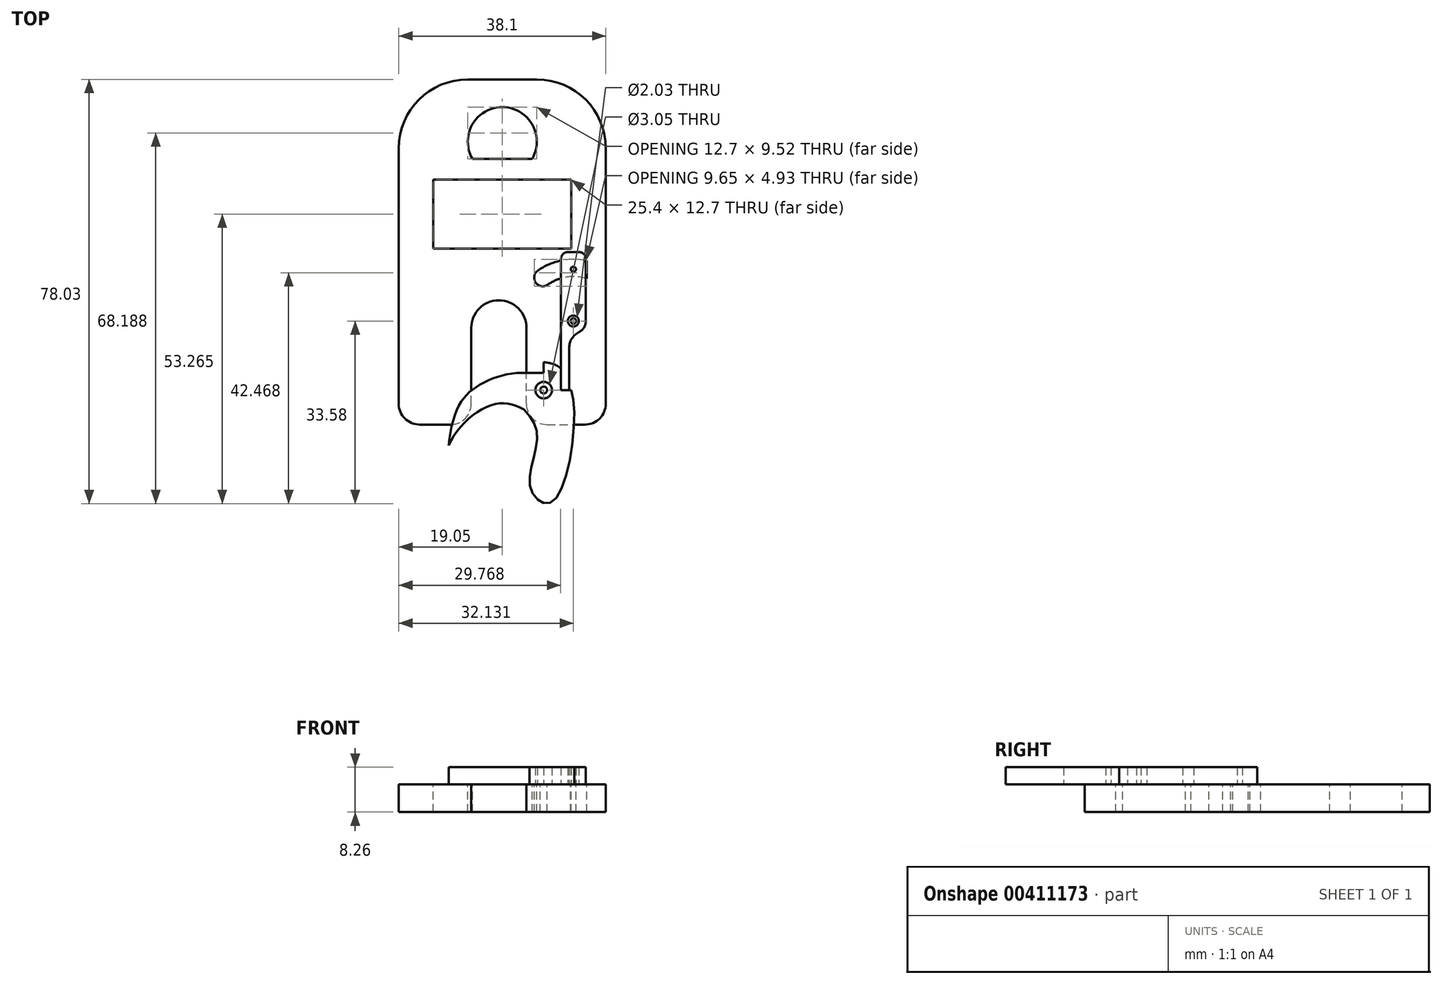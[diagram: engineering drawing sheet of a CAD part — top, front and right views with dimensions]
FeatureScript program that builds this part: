
annotation { "Feature Type Name" : "Feature", "Feature Type Description" : "" }
export const myFeature = defineFeature(function(context is Context, id is Id, definition is map)
    precondition{}
    {
        {
            var Q0;
            Q0=qCreatedBy(makeId("Top.planeOp"),FACE);
            var sketch = newSketch(context, id + "F0", { "sketchPlane" : qUnion([Q0])});
            skCircle(sketch, "E0", {"center": v(0, 0) * mm, "radius": 15.88 * mm, "construction": true});
            skEllipse(sketch, "E1", {"center": v(0, 0) * mm, "majorRadius": 12.7 * mm, "minorRadius": 7.62 * mm, "majorAxis": v(0.7, 0.7), "construction": true});
            skCircle(sketch, "E2", {"center": v(7.62, 7.62) * mm, "radius": 1.52 * mm});
            skLineSegment(sketch, "E3", {"start": v(-8.98, -8.98) * mm, "end": v(8.98, 8.98) * mm, "construction": true});
            skCircle(sketch, "E4", {"center": v(7.62, 7.62) * mm, "radius": 5.1 * mm, "construction": true});
            skLineSegment(sketch, "E5", {"start": v(12.72, 7.62) * mm, "end": v(10.8, 7.62) * mm});
            skLineSegment(sketch, "E6", {"start": v(10.8, 7.62) * mm, "end": v(10.8, 11.6) * mm});
            skArc(sketch, "E7", {"start": v(10.8, 11.6) * mm, "mid": v(9.3, 12.43) * mm, "end": v(7.62, 12.72) * mm});
            skCircle(sketch, "E8", {"center": v(7.62, 7.62) * mm, "radius": 2.98 * mm, "construction": true});
            skCircle(sketch, "E9", {"center": v(7.62, 7.62) * mm, "radius": 21.04 * mm, "construction": true});
            skFitSpline(sketch, "E10", {"points": [v(4.01, 4.01) * mm, v(-2.71, 1.83) * mm, v(-6.43, -8.04) * mm, v(-6.6, -9.02) * mm, v(-8.92, -8.19) * mm, v(-8.76, 2.93) * mm, v(-4.46, 8.4) * mm, v(3.63, 10.8) * mm], "startDerivative": vector(-47.69, -1.45) * mm, "endDerivative": vector(53.95, 0) * mm});
            skFitSpline(sketch, "E11.trimOffspring", {"points": [v(-10.38, -6.12) * mm, v(-1.13, 5.08) * mm, v(3.97, 4.05) * mm, v(4.01, 4.01) * mm, v(6.36, 0) * mm, v(5.13, -10.16) * mm, v(9.24, -12.9) * mm, v(12.72, 7.62) * mm], "startDerivative": vector(-10.72, 64.76) * mm, "endDerivative": vector(-17.22, 48.63) * mm});
            skLineSegment(sketch, "E12", {"start": v(3.63, 10.8) * mm, "end": v(7.62, 10.8) * mm});
            skLineSegment(sketch, "E13", {"start": v(7.62, 12.72) * mm, "end": v(7.62, 10.8) * mm});
            skLineSegment(sketch, "E14", {"start": v(7.62, 7.62) * mm, "end": v(7.62, 14.2) * mm, "construction": true});
            skSolve(sketch);
        }
        {
            var Q0;
            Q0=makeQuery(id+"F0.imprint","IMPRINT",FACE,{"disambiguationData":[TD([[makeQuery(id+"F0.imprint","IMPRINT",EDGE,{"derivedFrom":sQuery(id+"F0.wireOp",EDGE,"E2")}),-1.0]])]});
            extrude(context, id + "F1", {"entities" : qUnion([Q0]), "depth" : 3.17 * mm});
        }
        {
            var Q0;
            Q0=qCreatedBy(makeId("Top.planeOp"),FACE);
            var sketch = newSketch(context, id + "F2", { "sketchPlane" : qUnion([Q0])});
            skLineSegment(sketch, "E15.bottom", {"start": v(-6.35, 64.77) * mm, "end": v(6.35, 64.77) * mm});
            skLineSegment(sketch, "E15.top", {"start": v(-15.24, 1.27) * mm, "end": v(-9.53, 1.27) * mm});
            skLineSegment(sketch, "E15.left", {"start": v(-19.05, 52.07) * mm, "end": v(-19.05, 5.08) * mm});
            skLineSegment(sketch, "E15.right", {"start": v(19.05, 52.07) * mm, "end": v(19.05, 5.08) * mm});
            skLineSegment(sketch, "E16.top", {"start": v(-5.72, 19.05) * mm, "end": v(4.44, 19.05) * mm});
            skLineSegment(sketch, "E16.left", {"start": v(-5.72, 5.08) * mm, "end": v(-5.72, 19.05) * mm});
            skLineSegment(sketch, "E16.right", {"start": v(4.45, 5.08) * mm, "end": v(4.44, 19.05) * mm});
            skLineSegment(sketch, "E17", {"start": v(0, 0) * mm, "end": v(0, 39.33) * mm, "construction": true});
            skLineSegment(sketch, "E18.trimOffspring", {"start": v(8.26, 1.27) * mm, "end": v(15.24, 1.27) * mm});
            skCircle(sketch, "E19", {"center": v(7.62, 7.62) * mm, "radius": 0.64 * mm});
            skPoint(sketch, "E20.visualSharp", {"position": v(-19.05, 64.77) * mm});
            skArc(sketch, "E20.filletArc", {"start": v(-6.35, 64.77) * mm, "mid": v(-15.33, 61.05) * mm, "end": v(-19.05, 52.07) * mm});
            skPoint(sketch, "E21.visualSharp", {"position": v(19.05, 64.77) * mm});
            skArc(sketch, "E21.filletArc", {"start": v(19.05, 52.07) * mm, "mid": v(15.33, 61.05) * mm, "end": v(6.35, 64.77) * mm});
            skArc(sketch, "E22", {"start": v(5.5, 50.17) * mm, "mid": v(0, 59.7) * mm, "end": v(-5.5, 50.17) * mm});
            skLineSegment(sketch, "E23", {"start": v(-5.5, 50.17) * mm, "end": v(5.5, 50.17) * mm});
            skArc(sketch, "E24", {"start": v(4.44, 19.05) * mm, "mid": v(-0.64, 24.13) * mm, "end": v(-5.72, 19.05) * mm});
            skPoint(sketch, "E25.visualSharp", {"position": v(-19.05, 1.27) * mm});
            skArc(sketch, "E25.filletArc", {"start": v(-19.05, 5.08) * mm, "mid": v(-17.93, 2.39) * mm, "end": v(-15.24, 1.27) * mm});
            skPoint(sketch, "E26.visualSharp", {"position": v(-5.72, 1.27) * mm});
            skArc(sketch, "E26.filletArc", {"start": v(-9.53, 1.27) * mm, "mid": v(-6.83, 2.39) * mm, "end": v(-5.72, 5.08) * mm});
            skPoint(sketch, "E27.visualSharp", {"position": v(4.45, 1.27) * mm});
            skArc(sketch, "E27.filletArc", {"start": v(4.45, 5.08) * mm, "mid": v(5.56, 2.39) * mm, "end": v(8.26, 1.27) * mm});
            skPoint(sketch, "E28.visualSharp", {"position": v(19.05, 1.27) * mm});
            skArc(sketch, "E28.filletArc", {"start": v(15.24, 1.27) * mm, "mid": v(17.93, 2.39) * mm, "end": v(19.05, 5.08) * mm});
            skSolve(sketch);
        }
        {
            var Q0;
            Q0=makeQuery(id+"F2.imprint","IMPRINT",FACE,{"disambiguationData":[TD([[makeQuery(id+"F2.imprint","IMPRINT",EDGE,{"derivedFrom":sQuery(id+"F2.wireOp",EDGE,"E15.bottom")}),-1.0]])]});
            extrude(context, id + "F3", {"entities" : qUnion([Q0]), "oppositeDirection" : true, "depth" : 5.08 * mm});
        }
        {
            var Q0;
            Q0=makeQuery(id+"F3.opExtrude","CAP_FACE",FACE,{"disambiguationData":[OSD([sQuery(id+"F2.wireOp",EDGE,"E15.bottom"),sQuery(id+"F2.wireOp",EDGE,"E15.top"),sQuery(id+"F2.wireOp",EDGE,"E15.left"),sQuery(id+"F2.wireOp",EDGE,"E15.right"),sQuery(id+"F2.wireOp",EDGE,"E16.top"),sQuery(id+"F2.wireOp",EDGE,"E16.left"),sQuery(id+"F2.wireOp",EDGE,"E16.right"),sQuery(id+"F2.wireOp",EDGE,"E18.trimOffspring"),sQuery(id+"F2.wireOp",EDGE,"E19")])],"isStart":true});
            var sketch = newSketch(context, id + "F4", { "sketchPlane" : qUnion([Q0])});
            skLineSegment(sketch, "E29.bottom", {"start": v(10.8, 7.62) * mm, "end": v(12.32, 7.62) * mm});
            skLineSegment(sketch, "E29.top", {"start": v(12.06, 33.02) * mm, "end": v(14.1, 33.02) * mm});
            skLineSegment(sketch, "E29.left", {"start": v(10.8, 7.62) * mm, "end": v(10.8, 31.75) * mm});
            skLineSegment(sketch, "E29.right", {"start": v(15.37, 20.32) * mm, "end": v(15.37, 31.75) * mm});
            skLineSegment(sketch, "E30", {"start": v(13.08, 33.02) * mm, "end": v(13.08, 7.62) * mm, "construction": true});
            skCircle(sketch, "E31", {"center": v(13.08, 20.32) * mm, "radius": 1.02 * mm});
            skLineSegment(sketch, "E32", {"start": v(12.32, 7.62) * mm, "end": v(12.32, 15.42) * mm});
            skArc(sketch, "E33", {"start": v(14.1, 18.27) * mm, "mid": v(15.02, 19.11) * mm, "end": v(15.37, 20.32) * mm});
            skCircle(sketch, "E34", {"center": v(13.08, 29.85) * mm, "radius": 0.48 * mm});
            skPoint(sketch, "E35.orphan", {"position": v(15.37, 7.62) * mm});
            skPoint(sketch, "E36.visualSharp", {"position": v(12.32, 18.16) * mm});
            skArc(sketch, "E36.filletArc", {"start": v(14.1, 18.27) * mm, "mid": v(12.8, 17.1) * mm, "end": v(12.32, 15.42) * mm});
            skPoint(sketch, "E37.visualSharp", {"position": v(10.8, 33.02) * mm});
            skArc(sketch, "E37.filletArc", {"start": v(12.06, 33.02) * mm, "mid": v(11.17, 32.65) * mm, "end": v(10.8, 31.75) * mm});
            skPoint(sketch, "E38.visualSharp", {"position": v(15.37, 33.02) * mm});
            skArc(sketch, "E38.filletArc", {"start": v(15.37, 31.75) * mm, "mid": v(15, 32.65) * mm, "end": v(14.1, 33.02) * mm});
            skSolve(sketch);
        }
        {
            var Q0;
            Q0 = qSketchRegion(id + "F4", true);
            extrude(context, id + "F5", {"entities" : qUnion([Q0]), "depth" : 3.17 * mm});
        }
        {
            var Q0;
            Q0=sQuery(id+"F4.wireOp",VERTEX,"E33.center");
            var Q1;
            Q1=makeQuery(id+"F3.opExtrude","SWEPT_BODY",BODY,{"disambiguationData":[OSD([sQuery(id+"F2.wireOp",EDGE,"E15.bottom"),sQuery(id+"F2.wireOp",EDGE,"E15.top"),sQuery(id+"F2.wireOp",EDGE,"E15.left"),sQuery(id+"F2.wireOp",EDGE,"E15.right"),sQuery(id+"F2.wireOp",EDGE,"E16.top"),sQuery(id+"F2.wireOp",EDGE,"E16.left"),sQuery(id+"F2.wireOp",EDGE,"E16.right"),sQuery(id+"F2.wireOp",EDGE,"E18.trimOffspring"),sQuery(id+"F2.wireOp",EDGE,"E19")])]});
            hole(context, id + "F6", {"style" : HoleStyle.SIMPLE, "endStyle" : HoleEndStyle.THROUGH, "holeDiameter" : 1.02 * mm, "isTappedThrough" : true, "tappedDepth" : 12.7 * mm, "tapClearance" : 3, "locations" : qUnion([Q0]), "scope" : qUnion([Q1])});
        }
        {
            var Q0;
            Q0=makeQuery(id+"F3.opExtrude","CAP_FACE",FACE,{"disambiguationData":[OSD([sQuery(id+"F2.wireOp",EDGE,"E15.bottom"),sQuery(id+"F2.wireOp",EDGE,"E15.top"),sQuery(id+"F2.wireOp",EDGE,"E15.left"),sQuery(id+"F2.wireOp",EDGE,"E15.right"),sQuery(id+"F2.wireOp",EDGE,"E16.top"),sQuery(id+"F2.wireOp",EDGE,"E16.left"),sQuery(id+"F2.wireOp",EDGE,"E16.right"),sQuery(id+"F2.wireOp",EDGE,"E18.trimOffspring"),sQuery(id+"F2.wireOp",EDGE,"E19")])],"isStart":true});
            var sketch = newSketch(context, id + "F7", { "sketchPlane" : qUnion([Q0])});
            skArc(sketch, "E39", {"start": v(15.54, 31.4) * mm, "mid": v(10.85, 31.45) * mm, "end": v(6.54, 29.6) * mm});
            skArc(sketch, "E40", {"start": v(15.54, 28.12) * mm, "mid": v(11.83, 28.4) * mm, "end": v(8.37, 27) * mm});
            skArc(sketch, "E41", {"start": v(6.54, 29.6) * mm, "mid": v(6.16, 27.4) * mm, "end": v(8.37, 27) * mm});
            skLineSegment(sketch, "E42", {"start": v(15.54, 31.4) * mm, "end": v(15.54, 28.12) * mm});
            skSolve(sketch);
        }
        {
            var Q0;
            Q0=makeQuery(id+"F7.imprint","IMPRINT",FACE,{"disambiguationData":[TD([[makeQuery(id+"F7.imprint","IMPRINT",EDGE,{"derivedFrom":sQuery(id+"F7.wireOp",EDGE,"E39")}),1.0]])]});
            extrude(context, id + "F8", {"entities" : qUnion([Q0]), "operationType" : NewBodyOperationType.REMOVE, "oppositeDirection" : true, "depth" : 25.4 * mm});
        }
        {
            var Q0;
            Q0=makeQuery(id+"F3.opExtrude","CAP_FACE",FACE,{"disambiguationData":[OSD([sQuery(id+"F2.wireOp",EDGE,"E15.bottom"),sQuery(id+"F2.wireOp",EDGE,"E15.top"),sQuery(id+"F2.wireOp",EDGE,"E15.left"),sQuery(id+"F2.wireOp",EDGE,"E15.right"),sQuery(id+"F2.wireOp",EDGE,"E16.top"),sQuery(id+"F2.wireOp",EDGE,"E16.left"),sQuery(id+"F2.wireOp",EDGE,"E16.right"),sQuery(id+"F2.wireOp",EDGE,"E18.trimOffspring"),sQuery(id+"F2.wireOp",EDGE,"E19"),sQuery(id+"F2.wireOp",EDGE,"E20.filletArc"),sQuery(id+"F2.wireOp",EDGE,"E21.filletArc"),sQuery(id+"F2.wireOp",EDGE,"E22")])],"isStart":true});
            var sketch = newSketch(context, id + "F9", { "sketchPlane" : qUnion([Q0])});
            skLineSegment(sketch, "E43.bottom", {"start": v(12.7, 46.36) * mm, "end": v(-12.7, 46.36) * mm});
            skLineSegment(sketch, "E43.top", {"start": v(12.7, 33.66) * mm, "end": v(-12.7, 33.66) * mm});
            skLineSegment(sketch, "E43.left", {"start": v(12.7, 46.36) * mm, "end": v(12.7, 33.66) * mm});
            skLineSegment(sketch, "E43.right", {"start": v(-12.7, 46.36) * mm, "end": v(-12.7, 33.66) * mm});
            skPoint(sketch, "E43.middle", {"position": v(0, 40) * mm});
            skSolve(sketch);
        }
        {
            var Q0;
            Q0=makeQuery(id+"F9.imprint","IMPRINT",FACE,{"disambiguationData":[TD([[makeQuery(id+"F9.imprint","IMPRINT",EDGE,{"derivedFrom":sQuery(id+"F9.wireOp",EDGE,"E43.bottom")}),1.0]])]});
            extrude(context, id + "F10", {"entities" : qUnion([Q0]), "operationType" : NewBodyOperationType.REMOVE, "oppositeDirection" : true, "depth" : 25.4 * mm});
        }
    });
